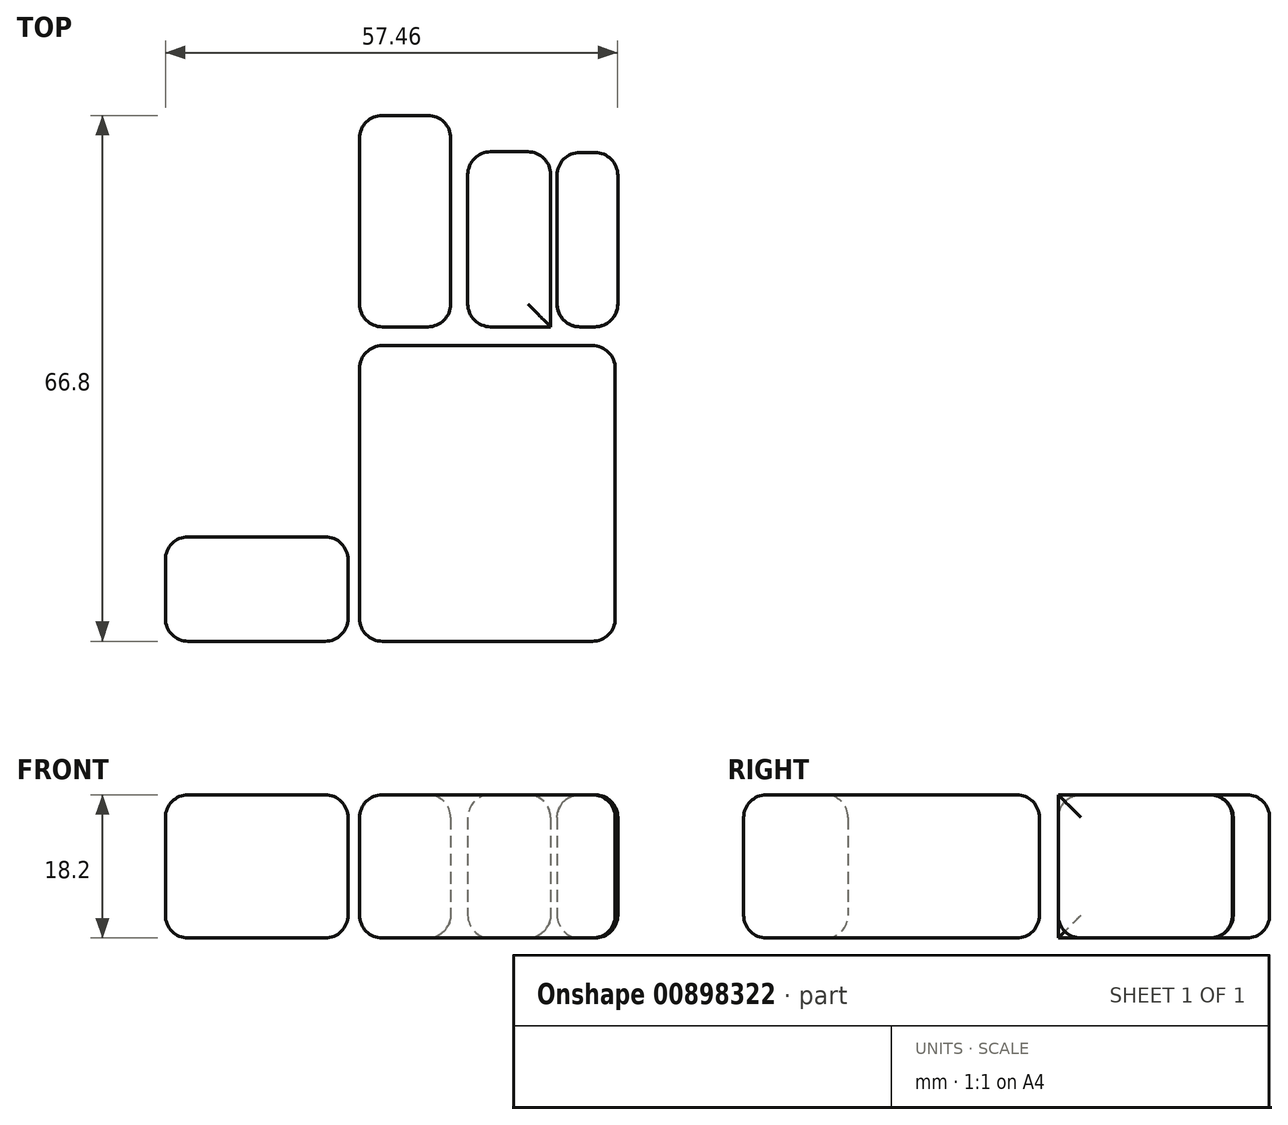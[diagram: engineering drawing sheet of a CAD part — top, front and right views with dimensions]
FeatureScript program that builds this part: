
annotation { "Feature Type Name" : "Feature", "Feature Type Description" : "" }
export const myFeature = defineFeature(function(context is Context, id is Id, definition is map)
    precondition{}
    {
        {
            var Q0;
            Q0=qCreatedBy(makeId("Top.planeOp"),FACE);
            var sketch = newSketch(context, id + "F0", { "sketchPlane" : qUnion([Q0])});
            skLineSegment(sketch, "E0.bottom", {"start": v(16.24, -18.78) * mm, "end": v(-16.24, -18.78) * mm});
            skLineSegment(sketch, "E0.top", {"start": v(16.24, 18.78) * mm, "end": v(-16.24, 18.78) * mm});
            skLineSegment(sketch, "E0.left", {"start": v(16.24, -18.78) * mm, "end": v(16.24, 18.78) * mm});
            skLineSegment(sketch, "E0.right", {"start": v(-16.24, -18.78) * mm, "end": v(-16.24, 18.78) * mm});
            skPoint(sketch, "E0.middle", {"position": v(0, 0) * mm});
            skLineSegment(sketch, "E1.bottom", {"start": v(-16.24, 21.17) * mm, "end": v(-4.67, 21.17) * mm});
            skLineSegment(sketch, "E1.top", {"start": v(-16.24, 48.02) * mm, "end": v(-4.67, 48.02) * mm});
            skLineSegment(sketch, "E1.left", {"start": v(-16.24, 21.17) * mm, "end": v(-16.24, 48.02) * mm});
            skLineSegment(sketch, "E1.right", {"start": v(-4.67, 21.17) * mm, "end": v(-4.67, 48.02) * mm});
            skLineSegment(sketch, "E2.bottom", {"start": v(-2.49, 21.17) * mm, "end": v(8.04, 21.17) * mm});
            skLineSegment(sketch, "E2.top", {"start": v(-2.49, 43.4) * mm, "end": v(8.04, 43.4) * mm});
            skLineSegment(sketch, "E2.left", {"start": v(-2.49, 21.17) * mm, "end": v(-2.49, 43.4) * mm});
            skLineSegment(sketch, "E2.right", {"start": v(8.04, 21.17) * mm, "end": v(8.04, 43.4) * mm});
            skLineSegment(sketch, "E3.bottom", {"start": v(8.85, 21.17) * mm, "end": v(16.56, 21.17) * mm});
            skLineSegment(sketch, "E3.top", {"start": v(8.85, 43.3) * mm, "end": v(16.56, 43.3) * mm});
            skLineSegment(sketch, "E3.left", {"start": v(8.85, 21.17) * mm, "end": v(8.85, 43.3) * mm});
            skLineSegment(sketch, "E3.right", {"start": v(16.56, 21.17) * mm, "end": v(16.56, 43.3) * mm});
            skLineSegment(sketch, "E4.bottom", {"start": v(-17.7, -18.78) * mm, "end": v(-40.9, -18.78) * mm});
            skLineSegment(sketch, "E4.top", {"start": v(-17.7, -5.51) * mm, "end": v(-40.9, -5.51) * mm});
            skLineSegment(sketch, "E4.left", {"start": v(-17.7, -18.78) * mm, "end": v(-17.7, -5.51) * mm});
            skLineSegment(sketch, "E4.right", {"start": v(-40.9, -18.78) * mm, "end": v(-40.9, -5.51) * mm});
            skSolve(sketch);
        }
        {
            var Q0;
            Q0 = qSketchRegion(id + "F0", true);
            extrude(context, id + "F1", {"entities" : qUnion([Q0]), "depth" : 18.2 * mm, "offsetDistance" : 25 * mm});
        }
        {
            var Q0;
            Q0=makeQuery(id+"F1.opExtrude","CAP_EDGE",EDGE,{"disambiguationData":[OSD([sQuery(id+"F0.wireOp",EDGE,"E1.top")])],"isStart":false});
            var Q1;
            Q1=makeQuery(id+"F1.opExtrude","SWEPT_EDGE",EDGE,{"disambiguationData":[OSD([sQuery(id+"F0.wireOp",EDGE,"E1.top"),sQuery(id+"F0.wireOp",EDGE,"E1.left")])]});
            var Q2;
            Q2=makeQuery(id+"F1.opExtrude","SWEPT_EDGE",EDGE,{"disambiguationData":[OSD([sQuery(id+"F0.wireOp",EDGE,"E1.top"),sQuery(id+"F0.wireOp",EDGE,"E1.right")])]});
            var Q3;
            Q3=makeQuery(id+"F1.opExtrude","CAP_EDGE",EDGE,{"disambiguationData":[OSD([sQuery(id+"F0.wireOp",EDGE,"E1.top")])],"isStart":true});
            var Q4;
            Q4=makeQuery(id+"F1.opExtrude","SWEPT_FACE",FACE,{"disambiguationData":[OSD([sQuery(id+"F0.wireOp",EDGE,"E3.top")])]});
            var Q5;
            Q5=makeQuery(id+"F1.opExtrude","SWEPT_FACE",FACE,{"disambiguationData":[OSD([sQuery(id+"F0.wireOp",EDGE,"E4.right")])]});
            var Q6;
            Q6=makeQuery(id+"F1.opExtrude","SWEPT_FACE",FACE,{"disambiguationData":[OSD([sQuery(id+"F0.wireOp",EDGE,"E4.top")])]});
            var Q7;
            Q7=makeQuery(id+"F1.opExtrude","CAP_FACE",FACE,{"disambiguationData":[OSD([sQuery(id+"F0.wireOp",EDGE,"E4.bottom"),sQuery(id+"F0.wireOp",EDGE,"E4.top"),sQuery(id+"F0.wireOp",EDGE,"E4.left"),sQuery(id+"F0.wireOp",EDGE,"E4.right")])],"isStart":false});
            var Q8;
            Q8=makeQuery(id+"F1.opExtrude","SWEPT_FACE",FACE,{"disambiguationData":[OSD([sQuery(id+"F0.wireOp",EDGE,"E4.bottom")])]});
            var Q9;
            Q9=makeQuery(id+"F1.opExtrude","CAP_FACE",FACE,{"disambiguationData":[OSD([sQuery(id+"F0.wireOp",EDGE,"E4.bottom"),sQuery(id+"F0.wireOp",EDGE,"E4.top"),sQuery(id+"F0.wireOp",EDGE,"E4.left"),sQuery(id+"F0.wireOp",EDGE,"E4.right")])],"isStart":true});
            var Q10;
            Q10=makeQuery(id+"F1.opExtrude","SWEPT_FACE",FACE,{"disambiguationData":[OSD([sQuery(id+"F0.wireOp",EDGE,"E1.left")])]});
            var Q11;
            Q11=makeQuery(id+"F1.opExtrude","CAP_FACE",FACE,{"disambiguationData":[OSD([sQuery(id+"F0.wireOp",EDGE,"E1.bottom"),sQuery(id+"F0.wireOp",EDGE,"E1.top"),sQuery(id+"F0.wireOp",EDGE,"E1.left"),sQuery(id+"F0.wireOp",EDGE,"E1.right")])],"isStart":false});
            var Q12;
            Q12=makeQuery(id+"F1.opExtrude","SWEPT_FACE",FACE,{"disambiguationData":[OSD([sQuery(id+"F0.wireOp",EDGE,"E1.right")])]});
            var Q13;
            Q13=makeQuery(id+"F1.opExtrude","SWEPT_FACE",FACE,{"disambiguationData":[OSD([sQuery(id+"F0.wireOp",EDGE,"E3.right")])]});
            var Q14;
            Q14=makeQuery(id+"F1.opExtrude","CAP_FACE",FACE,{"disambiguationData":[OSD([sQuery(id+"F0.wireOp",EDGE,"E3.bottom"),sQuery(id+"F0.wireOp",EDGE,"E3.top"),sQuery(id+"F0.wireOp",EDGE,"E3.left"),sQuery(id+"F0.wireOp",EDGE,"E3.right")])],"isStart":true});
            var Q15;
            Q15=makeQuery(id+"F1.opExtrude","SWEPT_FACE",FACE,{"disambiguationData":[OSD([sQuery(id+"F0.wireOp",EDGE,"E2.top")])]});
            var Q16;
            Q16=makeQuery(id+"F1.opExtrude","CAP_FACE",FACE,{"disambiguationData":[OSD([sQuery(id+"F0.wireOp",EDGE,"E2.bottom"),sQuery(id+"F0.wireOp",EDGE,"E2.top"),sQuery(id+"F0.wireOp",EDGE,"E2.left"),sQuery(id+"F0.wireOp",EDGE,"E2.right")])],"isStart":true});
            var Q17;
            Q17=makeQuery(id+"F1.opExtrude","SWEPT_FACE",FACE,{"disambiguationData":[OSD([sQuery(id+"F0.wireOp",EDGE,"E2.left")])]});
            var Q18;
            Q18=makeQuery(id+"F1.opExtrude","CAP_FACE",FACE,{"disambiguationData":[OSD([sQuery(id+"F0.wireOp",EDGE,"E2.bottom"),sQuery(id+"F0.wireOp",EDGE,"E2.top"),sQuery(id+"F0.wireOp",EDGE,"E2.left"),sQuery(id+"F0.wireOp",EDGE,"E2.right")])],"isStart":false});
            var Q19;
            Q19=makeQuery(id+"F1.opExtrude","SWEPT_FACE",FACE,{"disambiguationData":[OSD([sQuery(id+"F0.wireOp",EDGE,"E3.left")])]});
            var Q20;
            Q20=makeQuery(id+"F1.opExtrude","CAP_FACE",FACE,{"disambiguationData":[OSD([sQuery(id+"F0.wireOp",EDGE,"E0.bottom"),sQuery(id+"F0.wireOp",EDGE,"E0.top"),sQuery(id+"F0.wireOp",EDGE,"E0.left"),sQuery(id+"F0.wireOp",EDGE,"E0.right")])],"isStart":false});
            var Q21;
            Q21=makeQuery(id+"F1.opExtrude","SWEPT_FACE",FACE,{"disambiguationData":[OSD([sQuery(id+"F0.wireOp",EDGE,"E0.right")])]});
            var Q22;
            Q22=makeQuery(id+"F1.opExtrude","SWEPT_FACE",FACE,{"disambiguationData":[OSD([sQuery(id+"F0.wireOp",EDGE,"E0.left")])]});
            var Q23;
            Q23=makeQuery(id+"F1.opExtrude","CAP_FACE",FACE,{"disambiguationData":[OSD([sQuery(id+"F0.wireOp",EDGE,"E0.bottom"),sQuery(id+"F0.wireOp",EDGE,"E0.top"),sQuery(id+"F0.wireOp",EDGE,"E0.left"),sQuery(id+"F0.wireOp",EDGE,"E0.right")])],"isStart":true});
            var Q24;
            Q24=makeQuery(id+"F1.opExtrude","SWEPT_FACE",FACE,{"disambiguationData":[OSD([sQuery(id+"F0.wireOp",EDGE,"E0.bottom")])]});
            fillet(context, id + "F2", {"entities" : qUnion([Q0, Q1, Q2, Q3, Q4, Q5, Q6, Q7, Q8, Q9, Q10, Q11, Q12, Q13, Q14, Q15, Q16, Q17, Q18, Q19, Q20, Q21, Q22, Q23, Q24]), "radius" : 2.9 * mm, "tangentPropagation" : true, "allowEdgeOverflow" : false});
        }
    });
